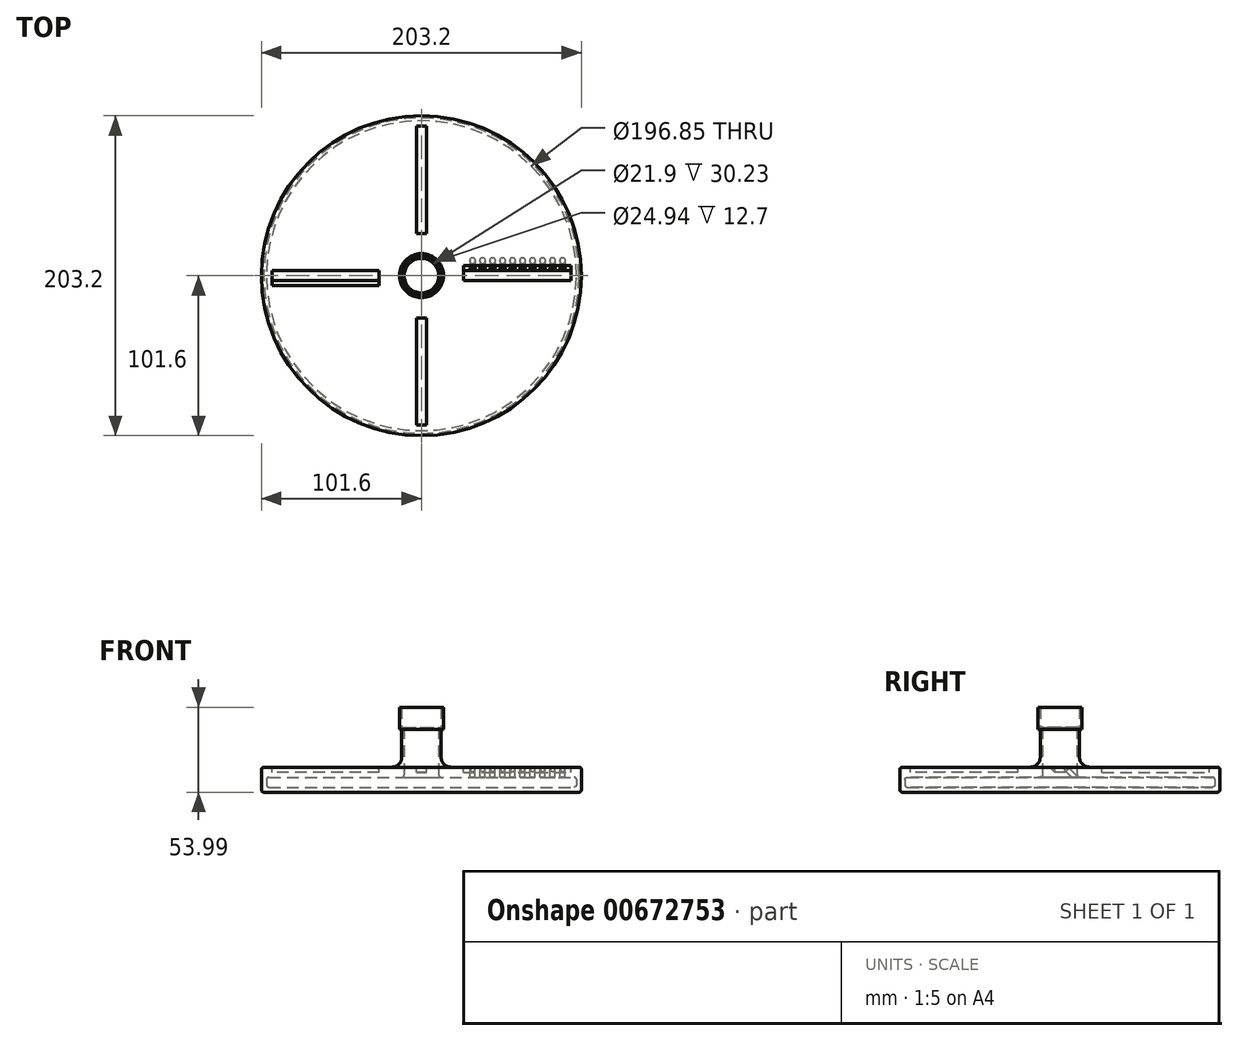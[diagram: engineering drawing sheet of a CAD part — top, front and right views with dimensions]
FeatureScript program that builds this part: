
annotation { "Feature Type Name" : "Feature", "Feature Type Description" : "" }
export const myFeature = defineFeature(function(context is Context, id is Id, definition is map)
    precondition{}
    {
        {
            var Q0;
            Q0=qCreatedBy(makeId("Front.planeOp"),FACE);
            var sketch = newSketch(context, id + "F0", { "sketchPlane" : qUnion([Q0])});
            skLineSegment(sketch, "E0", {"start": v(0, 0) * mm, "end": v(0, -54) * mm});
            skLineSegment(sketch, "E1", {"start": v(-12.47, 0) * mm, "end": v(-12.47, -12.7) * mm});
            skLineSegment(sketch, "E2", {"start": v(-12.47, -12.7) * mm, "end": v(-10.95, -12.7) * mm});
            skLineSegment(sketch, "E3", {"start": v(-10.95, -12.7) * mm, "end": v(-10.95, -38.1) * mm});
            skLineSegment(sketch, "E4", {"start": v(0, -76.2) * mm, "end": v(-101.6, -76.2) * mm});
            skLineSegment(sketch, "E5", {"start": v(-101.6, -52.47) * mm, "end": v(-101.6, -39.62) * mm});
            skLineSegment(sketch, "E6", {"start": v(-18.82, -38.1) * mm, "end": v(-100.08, -38.1) * mm});
            skLineSegment(sketch, "E7", {"start": v(-101.6, 29.96) * mm, "end": v(-98.43, 29.96) * mm});
            skLineSegment(sketch, "E8", {"start": v(-98.43, -44.45) * mm, "end": v(-98.43, -50.8) * mm});
            skLineSegment(sketch, "E9", {"start": v(-12.47, -44.45) * mm, "end": v(-96.9, -44.45) * mm});
            skLineSegment(sketch, "E10", {"start": v(-98.43, -45.97) * mm, "end": v(-98.43, -49.28) * mm});
            skLineSegment(sketch, "E11", {"start": v(-96.9, -50.8) * mm, "end": v(0, -50.8) * mm});
            skLineSegment(sketch, "E12", {"start": v(-12.47, 0) * mm, "end": v(-14, 0) * mm});
            skLineSegment(sketch, "E13", {"start": v(-14, 0) * mm, "end": v(-14, -12.7) * mm});
            skLineSegment(sketch, "E14", {"start": v(-12.47, -14.22) * mm, "end": v(-12.47, -31.75) * mm});
            skLineSegment(sketch, "E15", {"start": v(-10.95, -38.1) * mm, "end": v(-10.95, -36.58) * mm});
            skLineSegment(sketch, "E16", {"start": v(-14, -12.7) * mm, "end": v(-14, -14.22) * mm});
            skLineSegment(sketch, "E17", {"start": v(-14, -14.22) * mm, "end": v(-12.47, -14.22) * mm});
            skLineSegment(sketch, "E18", {"start": v(-10.95, -38.1) * mm, "end": v(-10.95, -39.62) * mm});
            skLineSegment(sketch, "E19", {"start": v(-10.95, -39.62) * mm, "end": v(-10.95, -42.93) * mm});
            skLineSegment(sketch, "E20.trimOffspring", {"start": v(-98.43, -76.2) * mm, "end": v(-98.43, -81.9) * mm});
            skPoint(sketch, "E21.visualSharp", {"position": v(-10.95, -44.45) * mm});
            skArc(sketch, "E21.filletArc", {"start": v(-12.47, -44.45) * mm, "mid": v(-11.4, -44) * mm, "end": v(-10.95, -42.93) * mm});
            skPoint(sketch, "E22.visualSharp", {"position": v(-98.43, -44.45) * mm});
            skArc(sketch, "E22.filletArc", {"start": v(-96.9, -44.45) * mm, "mid": v(-97.98, -44.9) * mm, "end": v(-98.43, -45.97) * mm});
            skPoint(sketch, "E23.visualSharp", {"position": v(-98.43, -50.8) * mm});
            skArc(sketch, "E23.filletArc", {"start": v(-98.43, -49.28) * mm, "mid": v(-97.98, -50.35) * mm, "end": v(-96.9, -50.8) * mm});
            skPoint(sketch, "E24.visualSharp", {"position": v(-101.6, -38.1) * mm});
            skArc(sketch, "E24.filletArc", {"start": v(-100.08, -38.1) * mm, "mid": v(-101.15, -38.55) * mm, "end": v(-101.6, -39.62) * mm});
            skPoint(sketch, "E25.visualSharp", {"position": v(-101.6, -53.98) * mm});
            skArc(sketch, "E25.filletArc", {"start": v(-101.6, -52.47) * mm, "mid": v(-101.18, -53.52) * mm, "end": v(-100.15, -54) * mm});
            skPoint(sketch, "E26.start.orphan", {"position": v(-98.43, -54) * mm});
            skLineSegment(sketch, "E27", {"start": v(-100.15, -54) * mm, "end": v(0, -54) * mm});
            skPoint(sketch, "E28.visualSharp", {"position": v(-12.47, -38.1) * mm});
            skArc(sketch, "E28.filletArc", {"start": v(-18.82, -38.1) * mm, "mid": v(-14.33, -36.24) * mm, "end": v(-12.47, -31.75) * mm});
            skLineSegment(sketch, "E29", {"start": v(0, 0) * mm, "end": v(0, 16.71) * mm});
            skSolve(sketch);
        }
        {
            var Q0;
            Q0=makeQuery(id+"F0.imprint","IMPRINT",FACE,{"disambiguationData":[TD([[makeQuery(id+"F0.imprint","IMPRINT",EDGE,{"derivedFrom":sQuery(id+"F0.wireOp",EDGE,"E1")}),-1.0]])]});
            var Q1;
            Q1 = qSketchRegion(id + "F2", true);
            var Q2;
            Q2=sQuery(id+"F0.wireOp",EDGE,"E29");
            revolve(context, id + "F1", {"entities" : qUnion([Q0, Q1]), "axis" : qUnion([Q2]), "revolveType" : RevolveType.FULL});
        }
        {
            var Q0;
            Q0=makeQuery(id+"F1.opRevolve","SWEPT_FACE",FACE,{"disambiguationData":[OSD([sQuery(id+"F0.wireOp",EDGE,"E6")])]});
            var sketch = newSketch(context, id + "F2", { "sketchPlane" : qUnion([Q0])});
            skLineSegment(sketch, "E30.0", {"start": v(-3.18, 0) * mm, "end": v(-3.18, -3.17) * mm});
            skArc(sketch, "E31", {"start": v(94.95, -3.17) * mm, "mid": v(95, 0) * mm, "end": v(94.95, 3.18) * mm});
            skLineSegment(sketch, "E32.trimOffspring", {"start": v(3.17, -26.81) * mm, "end": v(3.18, -94.95) * mm});
            skLineSegment(sketch, "E33.trimOffspring", {"start": v(-3.18, -26.81) * mm, "end": v(-3.17, -94.95) * mm});
            skArc(sketch, "E34.trimOffspring", {"start": v(-3.18, -94.95) * mm, "mid": v(0, -95) * mm, "end": v(3.17, -94.95) * mm});
            skLineSegment(sketch, "E35.trimOffspring", {"start": v(-26.81, 3.18) * mm, "end": v(-94.95, 3.17) * mm});
            skLineSegment(sketch, "E36.trimOffspring", {"start": v(-26.81, -3.17) * mm, "end": v(-94.95, -3.18) * mm});
            skLineSegment(sketch, "E37.trimOffspring", {"start": v(26.81, -3.18) * mm, "end": v(94.95, -3.17) * mm});
            skLineSegment(sketch, "E38.trimOffspring", {"start": v(26.81, 3.17) * mm, "end": v(94.95, 3.18) * mm});
            skArc(sketch, "E39.trimOffspring", {"start": v(3.17, 94.95) * mm, "mid": v(0, 95) * mm, "end": v(-3.17, 94.95) * mm});
            skArc(sketch, "E40.trimOffspring", {"start": v(-94.95, 3.17) * mm, "mid": v(-95, 0) * mm, "end": v(-94.95, -3.17) * mm});
            skLineSegment(sketch, "E41.trimOffspring", {"start": v(3.17, 26.81) * mm, "end": v(3.17, 94.95) * mm});
            skLineSegment(sketch, "E42.trimOffspring", {"start": v(-3.17, 26.81) * mm, "end": v(-3.17, 94.95) * mm});
            skLineSegment(sketch, "E43", {"start": v(-94.95, -3.18) * mm, "end": v(-94.95, 3.17) * mm});
            skLineSegment(sketch, "E44", {"start": v(-26.81, 3.18) * mm, "end": v(-26.81, -3.17) * mm});
            skLineSegment(sketch, "E45", {"start": v(-3.17, 26.81) * mm, "end": v(3.17, 26.81) * mm});
            skLineSegment(sketch, "E46", {"start": v(26.81, 3.17) * mm, "end": v(26.81, -3.18) * mm});
            skLineSegment(sketch, "E47", {"start": v(3.17, -26.81) * mm, "end": v(-3.18, -26.81) * mm});
            skSolve(sketch);
        }
        {
            var Q0;
            Q0 = qSketchRegion(id + "F2", true);
            extrude(context, id + "F3", {"entities" : qUnion([Q0]), "operationType" : NewBodyOperationType.REMOVE, "oppositeDirection" : true, "depth" : 3.17 * mm, "offsetDistance" : 25 * mm});
        }
        {
            var Q0;
            Q0=makeQuery(id+"F3.boolean.opBoolean","COPY",FACE,{"derivedFrom":makeQuery(id+"F3.opExtrude","SWEPT_FACE",FACE,{"disambiguationData":[OSD([sQuery(id+"F2.wireOp",EDGE,"E46")])]})});
            var sketch = newSketch(context, id + "F4", { "sketchPlane" : qUnion([Q0])});
            skLineSegment(sketch, "E48", {"start": v(3.18, -38.1) * mm, "end": v(6.35, -38.1) * mm});
            skLineSegment(sketch, "E49", {"start": v(3.18, -38.1) * mm, "end": v(3.18, -41.27) * mm});
            skLineSegment(sketch, "E50", {"start": v(3.18, -41.27) * mm, "end": v(6.35, -38.1) * mm});
            skSolve(sketch);
        }
        {
            var Q0;
            Q0 = qSketchRegion(id + "F4", true);
            extrude(context, id + "F5", {"entities" : qUnion([Q0]), "operationType" : NewBodyOperationType.REMOVE, "depth" : 68.2 * mm, "offsetDistance" : 25 * mm});
        }
        {
            var Q0;
            Q0=makeQuery(id+"F5.boolean.opBoolean","COPY",FACE,{"derivedFrom":makeQuery(id+"F5.opExtrude","SWEPT_FACE",FACE,{"disambiguationData":[OSD([sQuery(id+"F4.wireOp",EDGE,"E50")])]})});
            var sketch = newSketch(context, id + "F6", { "sketchPlane" : qUnion([Q0])});
            skLineSegment(sketch, "E51", {"start": v(26.81, -24.7) * mm, "end": v(95.01, -24.7) * mm});
            skLineSegment(sketch, "E52", {"start": v(26.81, -24.7) * mm, "end": v(32.46, -24.7) * mm});
            skLineSegment(sketch, "E53", {"start": v(32.46, -24.7) * mm, "end": v(38.81, -24.7) * mm});
            skLineSegment(sketch, "E54", {"start": v(38.81, -24.7) * mm, "end": v(45.16, -24.7) * mm});
            skLineSegment(sketch, "E55", {"start": v(45.16, -24.7) * mm, "end": v(51.51, -24.7) * mm});
            skLineSegment(sketch, "E56", {"start": v(51.51, -24.7) * mm, "end": v(57.86, -24.7) * mm});
            skLineSegment(sketch, "E57", {"start": v(57.86, -24.7) * mm, "end": v(64.21, -24.7) * mm});
            skLineSegment(sketch, "E58", {"start": v(64.21, -24.7) * mm, "end": v(70.56, -24.7) * mm});
            skLineSegment(sketch, "E59", {"start": v(70.56, -24.7) * mm, "end": v(76.91, -24.7) * mm});
            skLineSegment(sketch, "E60", {"start": v(76.91, -24.7) * mm, "end": v(83.26, -24.7) * mm});
            skCircle(sketch, "E61", {"center": v(32.46, -24.7) * mm, "radius": 1.5 * mm});
            skCircle(sketch, "E62", {"center": v(38.81, -24.7) * mm, "radius": 1.5 * mm});
            skCircle(sketch, "E63", {"center": v(45.16, -24.7) * mm, "radius": 1.5 * mm});
            skCircle(sketch, "E64", {"center": v(51.51, -24.7) * mm, "radius": 1.5 * mm});
            skCircle(sketch, "E65", {"center": v(57.86, -24.7) * mm, "radius": 1.5 * mm});
            skCircle(sketch, "E66", {"center": v(64.21, -24.7) * mm, "radius": 1.5 * mm});
            skCircle(sketch, "E67", {"center": v(70.56, -24.7) * mm, "radius": 1.5 * mm});
            skCircle(sketch, "E68", {"center": v(76.91, -24.7) * mm, "radius": 1.5 * mm});
            skCircle(sketch, "E69", {"center": v(83.26, -24.7) * mm, "radius": 1.5 * mm});
            skLineSegment(sketch, "E70", {"start": v(83.26, -24.7) * mm, "end": v(89.61, -24.7) * mm});
            skCircle(sketch, "E71", {"center": v(89.61, -24.7) * mm, "radius": 1.5 * mm});
            skSolve(sketch);
        }
        {
            var Q0;
            Q0 = qSketchRegion(id + "F6", true);
            extrude(context, id + "F7", {"entities" : qUnion([Q0]), "operationType" : NewBodyOperationType.REMOVE, "oppositeDirection" : true, "depth" : 9 * mm, "offsetDistance" : 25 * mm});
        }
        {
            var Q0;
            Q0=makeQuery(id+"F3.boolean.opBoolean","COPY",FACE,{"derivedFrom":makeQuery(id+"F3.opExtrude","SWEPT_FACE",FACE,{"disambiguationData":[OSD([sQuery(id+"F2.wireOp",EDGE,"E44")])]})});
            var sketch = newSketch(context, id + "F8", { "sketchPlane" : qUnion([Q0])});
            skLineSegment(sketch, "E72", {"start": v(3.17, -38.1) * mm, "end": v(3.17, -41.27) * mm});
            skLineSegment(sketch, "E73", {"start": v(3.17, -38.1) * mm, "end": v(6.35, -38.1) * mm});
            skLineSegment(sketch, "E74", {"start": v(3.17, -41.27) * mm, "end": v(6.35, -38.1) * mm});
            skSolve(sketch);
        }
        {
            var Q0;
            Q0 = qSketchRegion(id + "F8", true);
            extrude(context, id + "F9", {"entities" : qUnion([Q0]), "operationType" : NewBodyOperationType.REMOVE, "depth" : 68.2 * mm, "offsetDistance" : 25 * mm});
        }
    });
